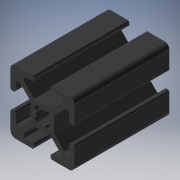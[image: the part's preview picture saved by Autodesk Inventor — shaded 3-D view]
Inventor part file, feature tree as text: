
AUTODESK INVENTOR PART (.ipt)
format: ipt  version: 2025 (Build 290162000, 162)  size: 237,056 bytes
history: native  units: mm
features: extrude x1, sketch x1
ambient origin geometry x8: Origin, YZ Plane, XZ Plane, XY Plane, X Axis, Y Axis, Z Axis, Center Point
bodies: Solid1 (feature_tree)
feature tree (2):
  extrude  "Extrusion1"  [1 undecoded]
  sketch  "Sketch_1"  dims[d0=30.0mm d1=0.0mm]
note: 1 required parameter value undecoded (feature->parameter linkage not recoverable at this tier; creation-order binding heuristic only, values carry confidence <= 0.55)
